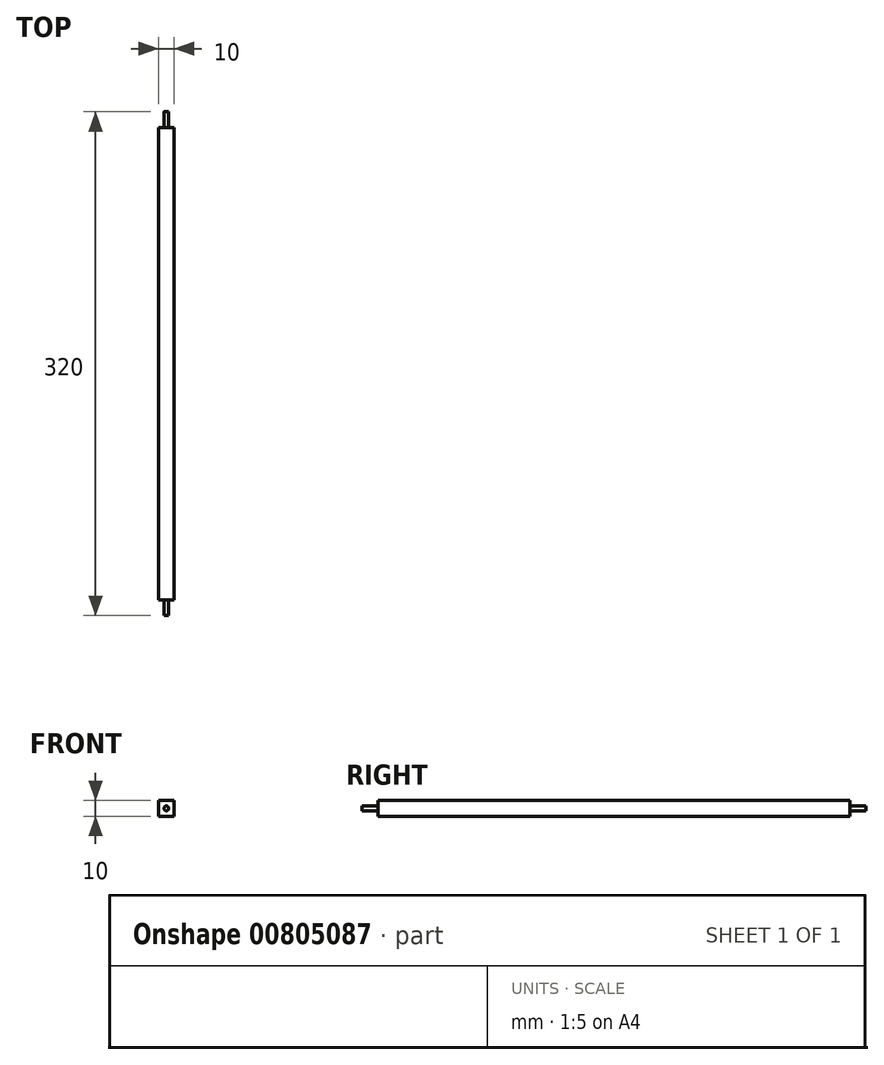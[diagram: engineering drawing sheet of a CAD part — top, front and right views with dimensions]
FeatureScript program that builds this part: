
annotation { "Feature Type Name" : "Feature", "Feature Type Description" : "" }
export const myFeature = defineFeature(function(context is Context, id is Id, definition is map)
    precondition{}
    {
        {
            var Q0;
            Q0=qCreatedBy(makeId("Right.planeOp"),FACE);
            var sketch = newSketch(context, id + "F0", { "sketchPlane" : qUnion([Q0])});
            skLineSegment(sketch, "E0.bottom", {"start": v(0, 10) * mm, "end": v(300, 10) * mm});
            skLineSegment(sketch, "E0.top", {"start": v(0, 0) * mm, "end": v(300, 0) * mm});
            skLineSegment(sketch, "E0.left", {"start": v(0, 10) * mm, "end": v(0, 0) * mm});
            skLineSegment(sketch, "E0.right", {"start": v(300, 10) * mm, "end": v(300, 0) * mm});
            skSolve(sketch);
        }
        {
            var Q0;
            Q0 = qSketchRegion(id + "F0", true);
            extrude(context, id + "F1", {"entities" : qUnion([Q0]), "endBound" : BoundingType.SYMMETRIC, "depth" : 10 * mm, "offsetDistance" : 25.4 * mm});
        }
        {
            var Q0;
            Q0=makeQuery(id+"F1.opExtrude","SWEPT_FACE",FACE,{"disambiguationData":[OSD([sQuery(id+"F0.wireOp",EDGE,"E0.left")])]});
            var sketch = newSketch(context, id + "F2", { "sketchPlane" : qUnion([Q0])});
            skCircle(sketch, "E1", {"center": v(0, 5) * mm, "radius": 1.5 * mm});
            skSolve(sketch);
        }
        {
            var Q0;
            Q0=makeQuery(id+"F2.imprint","IMPRINT",FACE,{"disambiguationData":[TD([[makeQuery(id+"F2.imprint","IMPRINT",EDGE,{"derivedFrom":sQuery(id+"F2.wireOp",EDGE,"E1")}),1.0]])]});
            var Q1;
            Q1=makeQuery(id+"F1.opExtrude","SWEPT_FACE",FACE,{"disambiguationData":[OSD([sQuery(id+"F0.wireOp",EDGE,"E0.right")])]});
            extrude(context, id + "F3", {"entities" : qUnion([Q0, Q1]), "operationType" : NewBodyOperationType.ADD, "depth" : 10 * mm, "offsetDistance" : 25 * mm});
        }
        {
            var Q0;
            Q0=makeQuery(id+"F1.opExtrude","SWEPT_FACE",FACE,{"disambiguationData":[OSD([sQuery(id+"F0.wireOp",EDGE,"E0.right")])]});
            var sketch = newSketch(context, id + "F4", { "sketchPlane" : qUnion([Q0])});
            skCircle(sketch, "E2", {"center": v(0, 5) * mm, "radius": 1.5 * mm});
            skSolve(sketch);
        }
        {
            var Q0;
            Q0=makeQuery(id+"F4.imprint","IMPRINT",FACE,{"disambiguationData":[TD([[makeQuery(id+"F4.imprint","IMPRINT",EDGE,{"derivedFrom":sQuery(id+"F4.wireOp",EDGE,"E2")}),1.0]])]});
            extrude(context, id + "F5", {"entities" : qUnion([Q0]), "operationType" : NewBodyOperationType.ADD, "depth" : 10 * mm, "offsetDistance" : 25 * mm});
        }
    });
